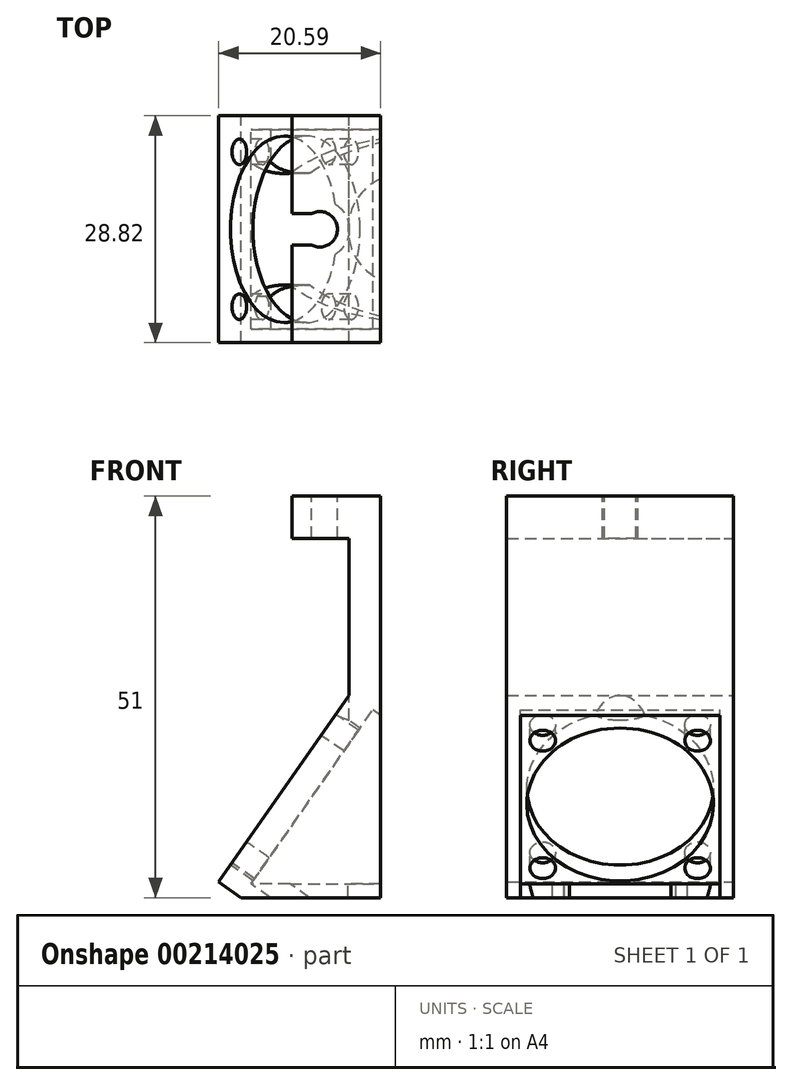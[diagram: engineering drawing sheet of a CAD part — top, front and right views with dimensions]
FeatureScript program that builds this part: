
annotation { "Feature Type Name" : "Feature", "Feature Type Description" : "" }
export const myFeature = defineFeature(function(context is Context, id is Id, definition is map)
    precondition{}
    {
        {
            var Q0;
            Q0=qCreatedBy(makeId("Front.planeOp"),FACE);
            var sketch = newSketch(context, id + "F0", { "sketchPlane" : qUnion([Q0])});
            skLineSegment(sketch, "E0", {"start": v(0, 0) * mm, "end": v(11.25, 0) * mm});
            skLineSegment(sketch, "E1", {"start": v(11.25, 0) * mm, "end": v(11.25, -25.7) * mm});
            skLineSegment(sketch, "E2", {"start": v(7.25, -25.3) * mm, "end": v(7.25, -5.34) * mm});
            skLineSegment(sketch, "E3", {"start": v(7.25, -5.34) * mm, "end": v(0, -5.34) * mm});
            skLineSegment(sketch, "E4", {"start": v(0, -5.34) * mm, "end": v(0, 0) * mm});
            skLineSegment(sketch, "E5", {"start": v(7.25, -25.3) * mm, "end": v(-9.34, -49) * mm});
            skLineSegment(sketch, "E6", {"start": v(-9.34, -49) * mm, "end": v(-6.47, -51) * mm});
            skLineSegment(sketch, "E7", {"start": v(-6.47, -51) * mm, "end": v(11.25, -25.7) * mm});
            skPoint(sketch, "E8.orphan", {"position": v(11.25, -28) * mm});
            skSolve(sketch);
        }
        {
            var Q0;
            Q0 = qSketchRegion(id + "F0", true);
            extrude(context, id + "F1", {"entities" : qUnion([Q0]), "depth" : (25.32 + (1.75 * 2)) * mm});
        }
        {
            var Q0;
            Q0=makeQuery(id+"F1.opExtrude","SWEPT_FACE",FACE,{"disambiguationData":[OSD([sQuery(id+"F0.wireOp",EDGE,"E0")])]});
            var sketch = newSketch(context, id + "F2", { "sketchPlane" : qUnion([Q0])});
            skLineSegment(sketch, "E9.0.0", {"start": v(0, 0) * mm, "end": v(7.25, 0) * mm, "construction": true});
            skLineSegment(sketch, "E9.0.1", {"start": v(7.25, 0) * mm, "end": v(7.25, -28.82) * mm, "construction": true});
            skLineSegment(sketch, "E9.0.2", {"start": v(7.25, -28.82) * mm, "end": v(0, -28.82) * mm, "construction": true});
            skLineSegment(sketch, "E9.0.3", {"start": v(0, -28.82) * mm, "end": v(0, 0) * mm, "construction": true});
            skLineSegment(sketch, "E10", {"start": v(7, 0) * mm, "end": v(7, -28.82) * mm, "construction": true});
            skLineSegment(sketch, "E11", {"start": v(7, 0) * mm, "end": v(0, -28.82) * mm, "construction": true});
            skArc(sketch, "E12", {"start": v(2.47, -16.41) * mm, "mid": v(5.75, -14.41) * mm, "end": v(2.47, -12.41) * mm});
            skLineSegment(sketch, "E13", {"start": v(2.47, -12.41) * mm, "end": v(0, -12.41) * mm});
            skLineSegment(sketch, "E14", {"start": v(0, -12.41) * mm, "end": v(0, -16.41) * mm});
            skLineSegment(sketch, "E15", {"start": v(0, -16.41) * mm, "end": v(2.47, -16.41) * mm});
            skPoint(sketch, "E16.trimOffspring.end.orphan", {"position": v(3.5, -16.41) * mm});
            skSolve(sketch);
        }
        {
            var Q0;
            Q0 = qSketchRegion(id + "F2", true);
            extrude(context, id + "F3", {"entities" : qUnion([Q0]), "operationType" : NewBodyOperationType.REMOVE, "oppositeDirection" : true, "depth" : 55.9 * mm});
        }
        {
            var Q0;
            Q0=makeQuery(id+"F1.opExtrude","SWEPT_FACE",FACE,{"disambiguationData":[OSD([sQuery(id+"F0.wireOp",EDGE,"E5")])]});
            var sketch = newSketch(context, id + "F4", { "sketchPlane" : qUnion([Q0])});
            skLineSegment(sketch, "E17.0", {"start": v(28.82, -16.57) * mm, "end": v(0, -16.57) * mm, "construction": true});
            skLineSegment(sketch, "E17.1", {"start": v(28.82, -16.57) * mm, "end": v(28.82, -45.49) * mm, "construction": true});
            skLineSegment(sketch, "E17.2", {"start": v(28.82, -45.49) * mm, "end": v(0, -45.49) * mm, "construction": true});
            skLineSegment(sketch, "E17.3", {"start": v(0, -16.57) * mm, "end": v(0, -45.49) * mm, "construction": true});
            skLineSegment(sketch, "E18.0", {"start": v(27.07, -18.32) * mm, "end": v(1.75, -18.32) * mm, "construction": true});
            skLineSegment(sketch, "E18.1", {"start": v(27.07, -18.32) * mm, "end": v(27.07, -43.74) * mm, "construction": true});
            skLineSegment(sketch, "E18.2", {"start": v(27.07, -43.74) * mm, "end": v(1.75, -43.74) * mm, "construction": true});
            skLineSegment(sketch, "E18.3", {"start": v(1.75, -18.32) * mm, "end": v(1.75, -43.74) * mm, "construction": true});
            skCircle(sketch, "E19", {"center": v(24.24, -21.14) * mm, "radius": 1.63 * mm});
            skLineSegment(sketch, "E20", {"start": v(27.07, -31.03) * mm, "end": v(1.75, -31.03) * mm, "construction": true});
            skLineSegment(sketch, "E21", {"start": v(14.4, -18.32) * mm, "end": v(14.4, -43.74) * mm, "construction": true});
            skCircle(sketch, "E22.MirrorC", {"center": v(24.24, -40.91) * mm, "radius": 1.63 * mm});
            skCircle(sketch, "E23.MirrorC", {"center": v(4.58, -21.14) * mm, "radius": 1.63 * mm});
            skCircle(sketch, "E24.MirrorC", {"center": v(4.58, -40.91) * mm, "radius": 1.63 * mm});
            skCircle(sketch, "E25", {"center": v(14.4, -31.03) * mm, "radius": 11.85 * mm});
            skSolve(sketch);
        }
        {
            var Q0;
            Q0 = qSketchRegion(id + "F4", true);
            extrude(context, id + "F5", {"entities" : qUnion([Q0]), "operationType" : NewBodyOperationType.REMOVE, "oppositeDirection" : true, "depth" : 25 * mm});
        }
        {
            var Q0;
            Q0=makeQuery(id+"F1.opExtrude","SWEPT_FACE",FACE,{"disambiguationData":[OSD([sQuery(id+"F0.wireOp",EDGE,"E3")])]});
            var sketch = newSketch(context, id + "F6", { "sketchPlane" : qUnion([Q0])});
            skArc(sketch, "E26.0", {"start": v(2.47, 12.41) * mm, "mid": v(5.75, 14.41) * mm, "end": v(2.47, 16.41) * mm});
            skCircle(sketch, "E27", {"center": v(3.5, 14.41) * mm, "radius": 3.75 * mm});
            skSolve(sketch);
        }
        {
            var Q0;
            Q0 = qSketchRegion(id + "F6", true);
            extrude(context, id + "F7", {"entities" : qUnion([Q0]), "operationType" : NewBodyOperationType.REMOVE, "depth" : 54.4 * mm});
        }
        {
            var Q0;
            Q0=makeQuery(id+"F1.opExtrude","SWEPT_FACE",FACE,{"disambiguationData":[OSD([sQuery(id+"F0.wireOp",EDGE,"E1"),sQuery(id+"F0.wireOp",EDGE,"Nfk5Y83t-zKs8-QYUL-KAzb-yZ28i0qq4Wyk")])]});
            var sketch = newSketch(context, id + "F8", { "sketchPlane" : qUnion([Q0])});
            skLineSegment(sketch, "E28.0", {"start": v(-28.82, -51) * mm, "end": v(-28.82, -25.7) * mm});
            skLineSegment(sketch, "E28.1", {"start": v(-28.82, -51) * mm, "end": v(0, -51) * mm});
            skLineSegment(sketch, "E28.2", {"start": v(0, -51) * mm, "end": v(0, -25.7) * mm});
            skLineSegment(sketch, "E29.0", {"start": v(-27.07, -49.25) * mm, "end": v(-27.07, -25.7) * mm});
            skLineSegment(sketch, "E29.1", {"start": v(-27.07, -49.25) * mm, "end": v(-1.75, -49.25) * mm});
            skLineSegment(sketch, "E29.2", {"start": v(-1.75, -49.25) * mm, "end": v(-1.75, -25.7) * mm});
            skLineSegment(sketch, "E30", {"start": v(-27.07, -25.7) * mm, "end": v(-28.82, -25.7) * mm});
            skLineSegment(sketch, "E31", {"start": v(-1.75, -25.7) * mm, "end": v(0, -25.7) * mm});
            skSolve(sketch);
        }
        {
            var Q0;
            Q0 = qSketchRegion(id + "F8", true);
            extrude(context, id + "F9", {"entities" : qUnion([Q0]), "operationType" : NewBodyOperationType.ADD, "endBound" : BoundingType.UP_TO_NEXT, "oppositeDirection" : true, "depth" : 25 * mm});
        }
        {
            var Q0;
            Q0=makeQuery(id+"F1.opExtrude","SWEPT_FACE",FACE,{"disambiguationData":[OSD([sQuery(id+"F0.wireOp",EDGE,"E7")])]});
            var sketch = newSketch(context, id + "F10", { "sketchPlane" : qUnion([Q0])});
            skCircle(sketch, "E32", {"center": v(-24.24, -40.91) * mm, "radius": 2.75 * mm});
            skLineSegment(sketch, "E33", {"start": v(-14.4, -43.35) * mm, "end": v(-14.4, -38.26) * mm});
            skCircle(sketch, "E34.MirrorC", {"center": v(-4.58, -40.91) * mm, "radius": 2.75 * mm});
            skSolve(sketch);
        }
        {
            var Q0;
            {var subQ1=makeQuery(id+"F1.opExtrude","SWEPT_FACE",FACE,{"disambiguationData":[OSD([sQuery(id+"F0.wireOp",EDGE,"E7")])]});Q0=makeQuery(id+"F10.imprint","IMPRINT",FACE,{"disambiguationData":[TD([[makeQuery(id+"F10.imprint","IMPRINT",EDGE,{"derivedFrom":makeQuery(id+"F5.boolean.opBoolean","INTERSECT",EDGE,{"derivedFrom":[subQ1,makeQuery(id+"F5.opExtrude","SWEPT_FACE",FACE,{"disambiguationData":[OSD([sQuery(id+"F4.wireOp",EDGE,"E22.MirrorC")])]})]})}),-1.0]])]});}
            var Q1;
            {var subQ0=sQuery(id+"F10.wireOp",EDGE,"E32");var subQ1=makeQuery(id+"F5.boolean.opBoolean","INTERSECT",EDGE,{"derivedFrom":[makeQuery(id+"F1.opExtrude","SWEPT_FACE",FACE,{"disambiguationData":[OSD([sQuery(id+"F0.wireOp",EDGE,"E7")])]}),makeQuery(id+"F5.opExtrude","SWEPT_FACE",FACE,{"disambiguationData":[OSD([sQuery(id+"F4.wireOp",EDGE,"E25")])]})]});var subQ2=makeQuery(id+"F10.imprint","INTERSECT",VERTEX,{"disambiguationData":[OD(0.0)],"derivedFrom":[subQ1,subQ0]});Q1=makeQuery(id+"F10.imprint","IMPRINT",FACE,{"disambiguationData":[TD([[makeQuery(id+"F10.imprint","IMPRINT",EDGE,{"disambiguationData":[TD([[subQ2,1.0]])],"derivedFrom":subQ0}),1.0]])]});}
            var Q2;
            {var subQ0=sQuery(id+"F10.wireOp",EDGE,"E34.MirrorC");var subQ1=makeQuery(id+"F5.boolean.opBoolean","INTERSECT",EDGE,{"derivedFrom":[makeQuery(id+"F1.opExtrude","SWEPT_FACE",FACE,{"disambiguationData":[OSD([sQuery(id+"F0.wireOp",EDGE,"E7")])]}),makeQuery(id+"F5.opExtrude","SWEPT_FACE",FACE,{"disambiguationData":[OSD([sQuery(id+"F4.wireOp",EDGE,"E25")])]})]});var subQ2=makeQuery(id+"F10.imprint","INTERSECT",VERTEX,{"disambiguationData":[OD(0.0)],"derivedFrom":[subQ1,subQ0]});Q2=makeQuery(id+"F10.imprint","IMPRINT",FACE,{"disambiguationData":[TD([[makeQuery(id+"F10.imprint","IMPRINT",EDGE,{"disambiguationData":[TD([[subQ2,1.0]])],"derivedFrom":subQ0}),-1.0]])]});}
            var Q3;
            {var subQ1=makeQuery(id+"F1.opExtrude","SWEPT_FACE",FACE,{"disambiguationData":[OSD([sQuery(id+"F0.wireOp",EDGE,"E7")])]});Q3=makeQuery(id+"F10.imprint","IMPRINT",FACE,{"disambiguationData":[TD([[makeQuery(id+"F10.imprint","IMPRINT",EDGE,{"derivedFrom":makeQuery(id+"F5.boolean.opBoolean","INTERSECT",EDGE,{"derivedFrom":[subQ1,makeQuery(id+"F5.opExtrude","SWEPT_FACE",FACE,{"disambiguationData":[OSD([sQuery(id+"F4.wireOp",EDGE,"E24.MirrorC")])]})]})}),1.0]])]});}
            var Q4;
            Q4=makeQuery(id+"F10.imprint","IMPRINT",FACE,{"disambiguationData":[TD([[makeQuery(id+"F10.imprint","IMPRINT",EDGE,{"derivedFrom":makeQuery(id+"F5.boolean.opBoolean","INTERSECT",EDGE,{"derivedFrom":[makeQuery(id+"F1.opExtrude","SWEPT_FACE",FACE,{"disambiguationData":[OSD([sQuery(id+"F0.wireOp",EDGE,"E7")])]}),makeQuery(id+"F5.opExtrude","SWEPT_FACE",FACE,{"disambiguationData":[OSD([sQuery(id+"F4.wireOp",EDGE,"E22.MirrorC")])]})]})}),1.0]])]});
            var Q5;
            Q5=makeQuery(id+"F10.imprint","IMPRINT",FACE,{"disambiguationData":[TD([[makeQuery(id+"F10.imprint","IMPRINT",EDGE,{"derivedFrom":makeQuery(id+"F5.boolean.opBoolean","INTERSECT",EDGE,{"derivedFrom":[makeQuery(id+"F1.opExtrude","SWEPT_FACE",FACE,{"disambiguationData":[OSD([sQuery(id+"F0.wireOp",EDGE,"E7")])]}),makeQuery(id+"F5.opExtrude","SWEPT_FACE",FACE,{"disambiguationData":[OSD([sQuery(id+"F4.wireOp",EDGE,"E24.MirrorC")])]})]})}),-1.0]])]});
            extrude(context, id + "F11", {"entities" : qUnion([Q0, Q1, Q2, Q3, Q4, Q5]), "operationType" : NewBodyOperationType.REMOVE, "depth" : 25 * mm});
        }
        {
            var Q0;
            Q0=makeQuery(id+"F1.opExtrude","SWEPT_FACE",FACE,{"disambiguationData":[OSD([sQuery(id+"F0.wireOp",EDGE,"E7")])]});
            var sketch = newSketch(context, id + "F12", { "sketchPlane" : qUnion([Q0])});
            skLineSegment(sketch, "E35", {"start": v(-1.75, -14.6) * mm, "end": v(-27.07, -14.6) * mm});
            skLineSegment(sketch, "E36", {"start": v(-27.07, -14.6) * mm, "end": v(-27.07, -16.34) * mm});
            skLineSegment(sketch, "E37", {"start": v(-27.07, -16.34) * mm, "end": v(-1.75, -16.34) * mm});
            skLineSegment(sketch, "E38", {"start": v(-1.75, -16.34) * mm, "end": v(-1.75, -14.6) * mm});
            skSolve(sketch);
        }
        {
            var Q0;
            Q0 = qSketchRegion(id + "F12", true);
            var Q1;
            Q1=makeQuery(id+"F9.boolean.opBoolean","MERGE",FACE,{"derivedFrom":[makeQuery(id+"F1.opExtrude","SWEPT_FACE",FACE,{"disambiguationData":[OSD([sQuery(id+"F0.wireOp",EDGE,"E1")])]}),makeQuery(id+"F9.opExtrude","CAP_FACE",FACE,{"disambiguationData":[OSD([sQuery(id+"F8.wireOp",EDGE,"E28.0"),sQuery(id+"F8.wireOp",EDGE,"E28.1"),sQuery(id+"F8.wireOp",EDGE,"E28.2"),sQuery(id+"F8.wireOp",EDGE,"E29.0"),sQuery(id+"F8.wireOp",EDGE,"E29.1"),sQuery(id+"F8.wireOp",EDGE,"E29.2"),sQuery(id+"F8.wireOp",EDGE,"E30"),sQuery(id+"F8.wireOp",EDGE,"E31")])],"isStart":true})]});
            extrude(context, id + "F13", {"entities" : qUnion([Q0]), "operationType" : NewBodyOperationType.ADD, "endBound" : BoundingType.UP_TO_SURFACE, "endBoundEntityFace" : qUnion([Q1]), "depth" : 25 * mm});
        }
        {
            var Q0;
            Q0=makeQuery(id+"F9.opExtrude","SWEPT_FACE",FACE,{"disambiguationData":[OSD([sQuery(id+"F8.wireOp",EDGE,"E29.1")])]});
            var sketch = newSketch(context, id + "F14", { "sketchPlane" : qUnion([Q0])});
            skLineSegment(sketch, "E39", {"start": v(7.1, -14.4) * mm, "end": v(11.25, -14.4) * mm});
            skArc(sketch, "E40", {"start": v(11.25, -7.97) * mm, "mid": v(7.1, -14.41) * mm, "end": v(11.25, -20.85) * mm});
            skLineSegment(sketch, "E41", {"start": v(11.25, -20.85) * mm, "end": v(11.25, -14.4) * mm});
            skLineSegment(sketch, "E42", {"start": v(11.25, -14.4) * mm, "end": v(11.25, -7.97) * mm});
            skSolve(sketch);
        }
        {
            var Q0;
            Q0 = qSketchRegion(id + "F14", true);
            extrude(context, id + "F15", {"entities" : qUnion([Q0]), "operationType" : NewBodyOperationType.REMOVE, "oppositeDirection" : true, "depth" : 25 * mm});
        }
    });
